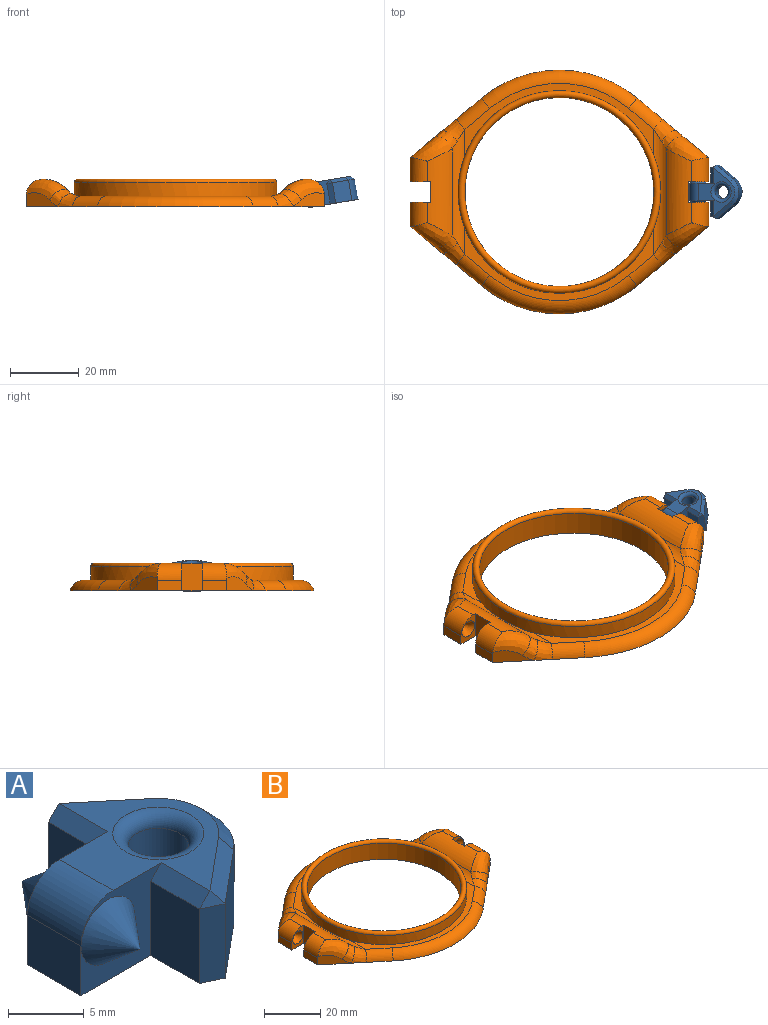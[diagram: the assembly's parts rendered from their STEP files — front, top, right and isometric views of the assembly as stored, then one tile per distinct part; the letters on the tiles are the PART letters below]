
ASSEMBLY  parts=2 mates=1
PART A: 24 faces, bbox 14.7x15.6x7 mm
  f0: plane 14.07x10.71mm, normal (0,0,1), area 48.6mm2, adj f2,f4,f13,f14,f17,f19,f20,f22
  f1: plane 6x4.54mm, normal (-1,0,0), area 27.2mm2, adj f2,f7,f14,f15
  f2: plane 7.5x7mm, normal (0,1,0), area 24.4mm2, adj f0,f1,f3,f7,f12,f14,f23
  f3: plane 5x4mm, normal (-1,0,0), area 20mm2, adj f2,f4,f7,f23
  f4: plane 7.5x7mm, normal (0,-1,0), area 24.4mm2, adj f0,f3,f5,f7,f11,f19,f23
  f5: plane 6x4.54mm, normal (-1,0,0), area 27.2mm2, adj f4,f7,f18,f19
  f6: plane 6x4.76mm, normal (0.64,0.77,0), area 37.2mm2, adj f7,f10,f15,f17
  f7: plane 15.61x14.71mm, normal (0,0,-1), area 109.4mm2, adj f1,f2,f3,f4,f5,f6,f8,f9
  f8: cylinder r=2mm len=6mm, axis (0,0,-1), area 75.4mm2, adj f7,f13
  f9: plane 6x4.76mm, normal (0.64,-0.77,0), area 37.2mm2, adj f7,f10,f18,f22
  f10: cylinder r=5mm len=7.69mm, axis (0,0,-1), area 52.6mm2, adj f6,f7,f9,f20
  f11: cone r=0mm half-angle=39.8deg, axis (0,1,0), area 30.7mm2, adj f4
  f12: cone r=0mm half-angle=39.8deg, axis (0,-1,0), area 30.7mm2, adj f2
  f13: torus R=3mm, axis (0,0,1), area 23.3mm2, adj f0,f8
  f14: plane 4.54x1mm, normal (-0.71,0,0.71), area 6.4mm2, adj f0,f1,f2,f16
  f15: plane 6x1.64mm, normal (-0.42,0.91,0), area 10.9mm2, adj f1,f6,f7,f16
  f16: plane 1.64x1mm, normal (-0.39,0.83,0.39), area 1mm2, adj f14,f15,f17
  f17: plane 5.4x4.73mm, normal (0.45,0.54,0.71), area 8.8mm2, adj f0,f6,f16,f20
  f18: plane 6x1.64mm, normal (-0.42,-0.91,0), area 10.9mm2, adj f5,f7,f9,f21
  f19: plane 4.54x1mm, normal (-0.71,0,0.71), area 6.4mm2, adj f0,f4,f5,f21
  f20: cone r=4mm half-angle=45deg, axis (0,0,-1), area 11.2mm2, adj f0,f10,f17,f22
  f21: plane 1.64x1mm, normal (-0.39,-0.83,0.39), area 1mm2, adj f18,f19,f22
  f22: plane 5.4x4.73mm, normal (0.45,-0.54,0.71), area 8.8mm2, adj f0,f9,f20,f21
  f23: cylinder r=3mm len=5mm, axis (0,1,0), area 23.6mm2, adj f0,f2,f3,f4
PART B: 50 faces, bbox 89.2x77.2x9.6 mm
  f0: plane 55x20.95mm, normal (0,0,1), area 157.2mm2, adj f21,f23,f24,f44,f45,f46
  f1: plane 9.33x7.76mm, normal (-0.64,0.77,0), area 34mm2, adj f4,f16,f27,f32,f33
  f2: plane 9.33x7.76mm, normal (0.64,-0.77,0), area 34mm2, adj f10,f16,f25,f48,f49
  f3: plane 9.33x7.76mm, normal (0.64,0.77,0), area 34mm2, adj f15,f16,f28,f39,f40
  f4: plane 7x3mm, normal (-1,0,0), area 21mm2, adj f1,f5,f16,f27
  f5: plane 8x6mm, normal (0,-1,0), area 21.6mm2, adj f4,f6,f16,f20,f27,f30
  f6: plane 7.93x6mm, normal (-1,0,0), area 47.6mm2, adj f5,f7,f16,f30
  f7: plane 8x6mm, normal (0,1,0), area 21.6mm2, adj f6,f8,f16,f19,f26,f30
  f8: plane 7x3mm, normal (-1,0,0), area 21mm2, adj f7,f9,f16,f26
  f9: plane 9.33x7.76mm, normal (-0.64,-0.77,0), area 34mm2, adj f8,f16,f26,f41,f42
  f10: plane 7x3mm, normal (1,0,0), area 21mm2, adj f2,f11,f16,f25
  f11: plane 8x6mm, normal (0,1,0), area 21.6mm2, adj f10,f12,f16,f18,f25,f29
  f12: plane 7.93x6mm, normal (1,0,0), area 47.6mm2, adj f11,f13,f16,f29
  f13: plane 8x6mm, normal (0,-1,0), area 21.6mm2, adj f12,f15,f16,f17,f28,f29
  f14: cylinder r=27.5mm len=55mm, axis (0,0,-1), area 1209.5mm2, adj f16,f31
  f15: plane 7x3mm, normal (1,0,0), area 21mm2, adj f3,f13,f16,f28
  f16: plane 87.1x71.1mm, normal (0,0,-1), area 2091.4mm2, adj f1,f2,f3,f4,f5,f6,f7,f8
  f17: cone r=0mm half-angle=39.8deg, axis (0,-1,0), area 32.7mm2, adj f13
  f18: cone r=0mm half-angle=39.8deg, axis (0,1,0), area 32.7mm2, adj f11
  f19: cone r=0mm half-angle=39.8deg, axis (0,1,0), area 32.7mm2, adj f7
  f20: cone r=0mm half-angle=39.8deg, axis (0,-1,0), area 32.7mm2, adj f5
  f21: cylinder r=29.5mm len=59mm, axis (0,0,1), area 736.9mm2, adj f0,f22,f23,f24,f31
  f22: plane 55x20.95mm, normal (0,0,1), area 157.2mm2, adj f21,f23,f24,f35,f36,f37
  f23: cylinder r=5mm len=36.53mm, axis (0,1,0), area 106.1mm2, adj f0,f21,f22,f29,f38,f39,f47,f48
  f24: cylinder r=5mm len=36.53mm, axis (0,-1,0), area 98.8mm2, adj f0,f21,f22,f30,f33,f34,f42,f43
  f25: cylinder r=5mm len=7.08mm, axis (0,-1,0), area 53mm2, adj f2,f10,f11,f29,f49
  f26: cylinder r=5mm len=7.08mm, axis (0,1,0), area 53mm2, adj f7,f8,f9,f30,f41
  f27: cylinder r=5mm len=7.08mm, axis (0,1,0), area 53mm2, adj f1,f4,f5,f30,f32
  f28: cylinder r=5mm len=7.08mm, axis (0,-1,0), area 53mm2, adj f3,f13,f15,f29,f40
  f29: cylinder r=10mm len=25.05mm, axis (0,-1,0), area 170.3mm2, adj f11,f12,f13,f23,f25,f28,f40,f49
  f30: cylinder r=10mm len=25.05mm, axis (0,-1,0), area 170.3mm2, adj f5,f6,f7,f24,f26,f27,f32,f41
  f31: torus R=28.5mm, axis (0,0,1), area 562.6mm2, adj f14,f21
  f32: bspline ~14.09x12.6mm, area 70.4mm2, adj f1,f27,f30,f33
  f33: bspline ~6.98x5.36mm, area 23.6mm2, adj f1,f24,f32,f34
  f34: bspline ~7.08x7.05mm, area 27.8mm2, adj f16,f24,f33,f35
  f35: cylinder r=4mm len=9.76mm, axis (0.77,0.64,0), area 49.9mm2, adj f16,f22,f34,f36
  f36: torus R=31.63mm, axis (0,0,-1), area 248mm2, adj f16,f22,f35,f37
  f37: cylinder r=4mm len=9.76mm, axis (-0.77,0.64,0), area 49.9mm2, adj f16,f22,f36,f38
  f38: bspline ~7.08x7.05mm, area 27.8mm2, adj f16,f23,f37,f39
  f39: bspline ~6.98x5.36mm, area 23.6mm2, adj f3,f23,f38,f40
  f40: bspline ~14.09x12.6mm, area 70.4mm2, adj f3,f28,f29,f39
  f41: bspline ~14.09x12.6mm, area 70.4mm2, adj f9,f26,f30,f42
  f42: bspline ~6.98x5.36mm, area 23.6mm2, adj f9,f24,f41,f43
  f43: bspline ~7.08x7.05mm, area 27.8mm2, adj f16,f24,f42,f44
  f44: cylinder r=4mm len=9.76mm, axis (0.77,-0.64,0), area 49.9mm2, adj f0,f16,f43,f45
  f45: torus R=31.63mm, axis (0,0,-1), area 248mm2, adj f0,f16,f44,f46
  f46: cylinder r=4mm len=9.76mm, axis (-0.77,-0.64,0), area 49.9mm2, adj f0,f16,f45,f47
  f47: bspline ~7.08x7.05mm, area 27.8mm2, adj f16,f23,f46,f48
  f48: bspline ~6.98x5.36mm, area 23.6mm2, adj f2,f23,f47,f49
  f49: bspline ~14.09x12.6mm, area 70.4mm2, adj f2,f25,f29,f48
PLACE A rot(axis=(0,-1,0),9.6deg) t=(1.24,0,-6.71)mm
PLACE B at identity
MATE revolute B.f17 <-> A.f11  axis (0,-1,0) through (40.5,3,4)mm
